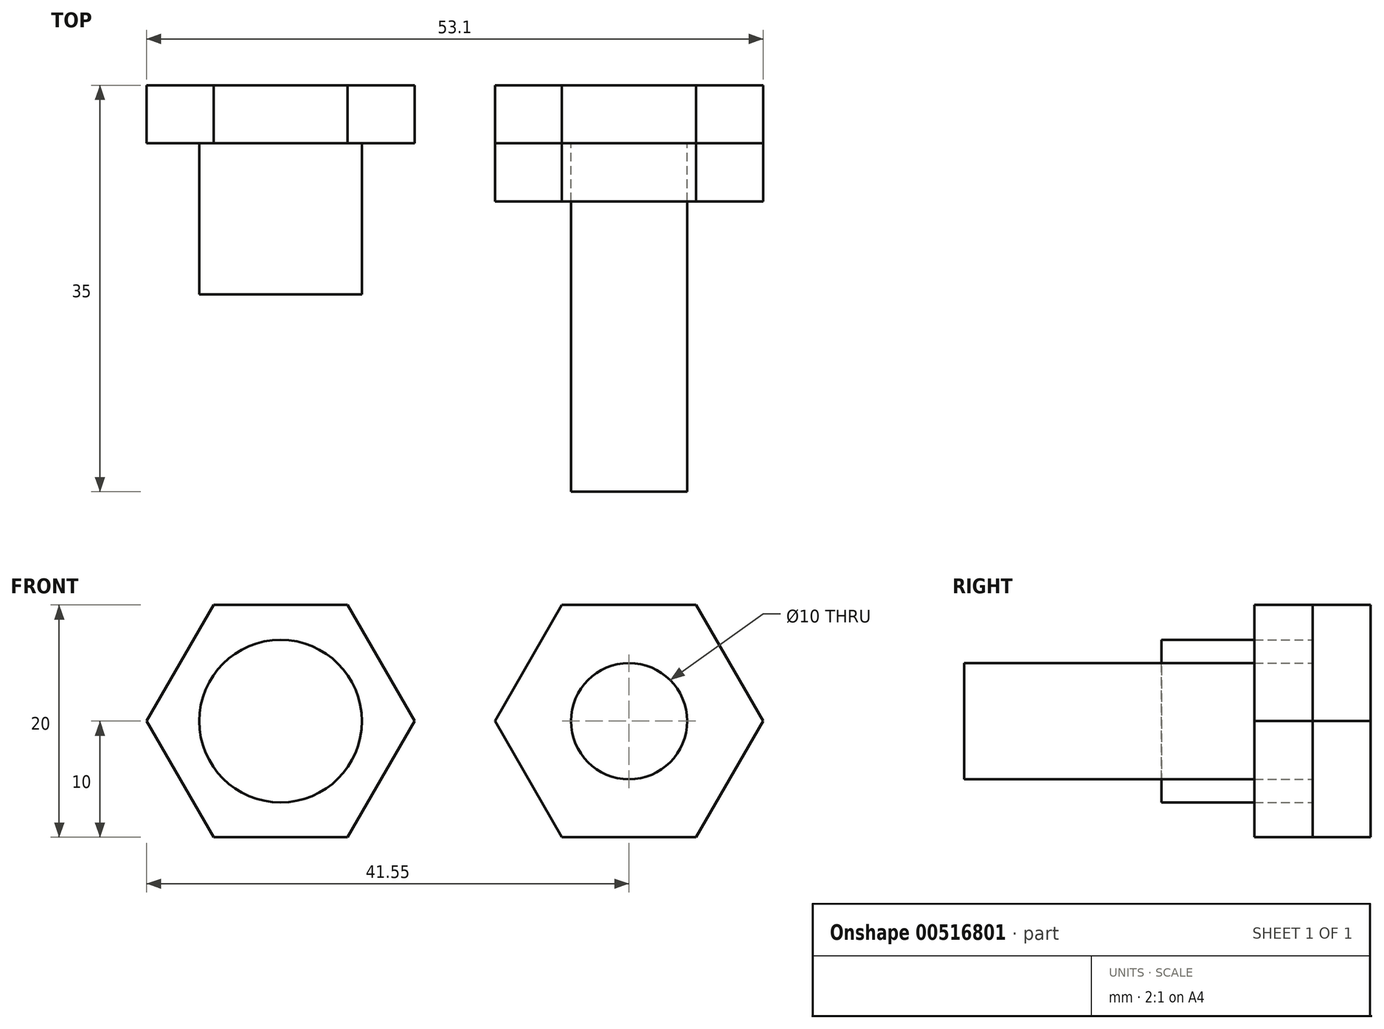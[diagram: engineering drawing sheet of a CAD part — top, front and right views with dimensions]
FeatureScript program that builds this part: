
annotation { "Feature Type Name" : "Feature", "Feature Type Description" : "" }
export const myFeature = defineFeature(function(context is Context, id is Id, definition is map)
    precondition{}
    {
        {
            var Q0;
            Q0=qCreatedBy(makeId("Front.planeOp"),FACE);
            var sketch = newSketch(context, id + "F0", { "sketchPlane" : qUnion([Q0])});
            skCircle(sketch, "E0.cCircle", {"center": v(0, 0) * mm, "radius": 10 * mm, "construction": true});
            skLineSegment(sketch, "E0.0", {"start": v(-5.77, 10) * mm, "end": v(5.77, 10) * mm});
            skLineSegment(sketch, "E0.1", {"start": v(5.77, 10) * mm, "end": v(11.55, 0) * mm});
            skLineSegment(sketch, "E0.2", {"start": v(11.55, 0) * mm, "end": v(5.77, -10) * mm});
            skLineSegment(sketch, "E0.3", {"start": v(5.77, -10) * mm, "end": v(-5.77, -10) * mm});
            skLineSegment(sketch, "E0.4", {"start": v(-5.77, -10) * mm, "end": v(-11.55, 0) * mm});
            skLineSegment(sketch, "E0.5", {"start": v(-11.55, 0) * mm, "end": v(-5.77, 10) * mm});
            skPoint(sketch, "E0.0.midPoint", {"position": v(0, 10) * mm});
            skCircle(sketch, "E1.cCircle", {"center": v(30, 0) * mm, "radius": 10 * mm, "construction": true});
            skLineSegment(sketch, "E1.0", {"start": v(24.23, 10) * mm, "end": v(35.77, 10) * mm});
            skLineSegment(sketch, "E1.1", {"start": v(35.77, 10) * mm, "end": v(41.55, 0) * mm});
            skLineSegment(sketch, "E1.2", {"start": v(41.55, 0) * mm, "end": v(35.77, -10) * mm});
            skLineSegment(sketch, "E1.3", {"start": v(35.77, -10) * mm, "end": v(24.23, -10) * mm});
            skLineSegment(sketch, "E1.4", {"start": v(24.23, -10) * mm, "end": v(18.45, 0) * mm});
            skLineSegment(sketch, "E1.5", {"start": v(18.45, 0) * mm, "end": v(24.23, 10) * mm});
            skPoint(sketch, "E1.0.midPoint", {"position": v(30, 10) * mm});
            skCircle(sketch, "E2", {"center": v(0, 0) * mm, "radius": 7 * mm});
            skCircle(sketch, "E3", {"center": v(30, 0) * mm, "radius": 5 * mm});
            skLineSegment(sketch, "E4", {"start": v(30, 0) * mm, "end": v(30, 5) * mm, "construction": true});
            skLineSegment(sketch, "E5", {"start": v(30, 5) * mm, "end": v(30, 10) * mm, "construction": true});
            skSolve(sketch);
        }
        {
            var Q0;
            Q0=makeQuery(id+"F0.imprint","IMPRINT",FACE,{"disambiguationData":[TD([[makeQuery(id+"F0.imprint","IMPRINT",EDGE,{"derivedFrom":sQuery(id+"F0.wireOp",EDGE,"E3")}),1.0]])]});
            extrude(context, id + "F1", {"entities" : qUnion([Q0]), "depth" : 30 * mm, "offsetDistance" : 25 * mm});
        }
        {
            var Q0;
            Q0=makeQuery(id+"F0.imprint","IMPRINT",FACE,{"disambiguationData":[TD([[makeQuery(id+"F0.imprint","IMPRINT",EDGE,{"derivedFrom":sQuery(id+"F0.wireOp",EDGE,"E2")}),1.0]])]});
            extrude(context, id + "F2", {"entities" : qUnion([Q0]), "depth" : 13 * mm, "offsetDistance" : 25 * mm});
        }
        {
            var Q0;
            Q0=makeQuery(id+"F0.imprint","IMPRINT",FACE,{"disambiguationData":[TD([[makeQuery(id+"F0.imprint","IMPRINT",EDGE,{"derivedFrom":sQuery(id+"F0.wireOp",EDGE,"E0.0")}),-1.0]])]});
            var Q1;
            Q1=makeQuery(id+"F0.imprint","IMPRINT",FACE,{"disambiguationData":[TD([[makeQuery(id+"F0.imprint","IMPRINT",EDGE,{"derivedFrom":sQuery(id+"F0.wireOp",EDGE,"E2")}),1.0]])]});
            var Q2;
            Q2=makeQuery(id+"F0.imprint","IMPRINT",FACE,{"disambiguationData":[TD([[makeQuery(id+"F0.imprint","IMPRINT",EDGE,{"derivedFrom":sQuery(id+"F0.wireOp",EDGE,"E1.0")}),-1.0]])]});
            var Q3;
            Q3=makeQuery(id+"F0.imprint","IMPRINT",FACE,{"disambiguationData":[TD([[makeQuery(id+"F0.imprint","IMPRINT",EDGE,{"derivedFrom":sQuery(id+"F0.wireOp",EDGE,"E3")}),1.0]])]});
            extrude(context, id + "F3", {"entities" : qUnion([Q0, Q1, Q2, Q3]), "operationType" : NewBodyOperationType.ADD, "oppositeDirection" : true, "depth" : 5 * mm, "offsetDistance" : 25 * mm});
        }
        {
            var Q0;
            Q0=makeQuery(id+"F0.imprint","IMPRINT",FACE,{"disambiguationData":[TD([[makeQuery(id+"F0.imprint","IMPRINT",EDGE,{"derivedFrom":sQuery(id+"F0.wireOp",EDGE,"E1.0")}),-1.0]])]});
            extrude(context, id + "F4", {"entities" : qUnion([Q0]), "depth" : 5 * mm, "offsetDistance" : 25 * mm});
        }
    });
